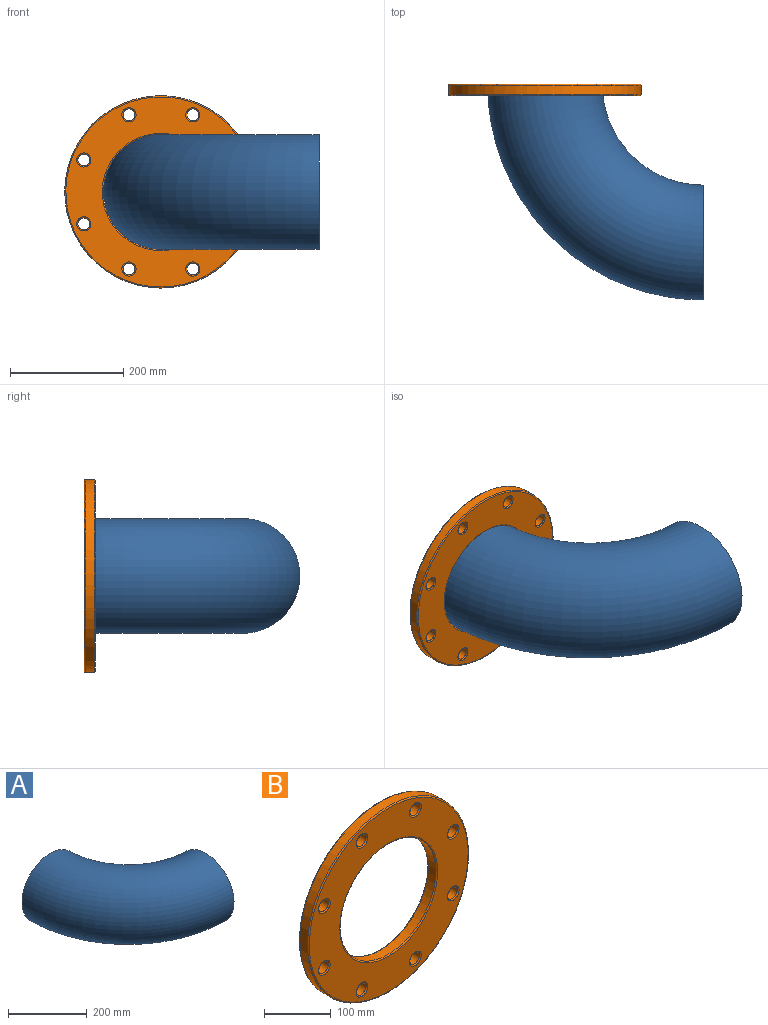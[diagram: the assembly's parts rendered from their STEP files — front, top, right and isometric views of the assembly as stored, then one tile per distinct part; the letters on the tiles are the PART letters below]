
ASSEMBLY  parts=2 mates=1
PART A: 4 faces, bbox 412.7x412.7x203 mm
  f0: torus R=279.76mm, axis (0,0,1), area 269205.5mm2, adj f1,f2
  f1: plane 203x203mm, normal (0,1,0), area 2500.7mm2, adj f0,f3
  f2: plane 203x203mm, normal (1,0,0), area 2500.7mm2, adj f0,f3
  f3: torus R=279.76mm, axis (0,0,1), area 280249.8mm2, adj f1,f2
PART B: 32 faces, bbox 368x20x368 mm
  f0: cylinder r=101.6mm len=203.2mm, axis (0,1,0), area 10213.9mm2, adj f20,f30
  f1: cylinder r=10.5mm len=21mm, axis (0,1,0), area 1055.6mm2, adj f19,f29
  f2: cylinder r=10.5mm len=21mm, axis (0,1,0), area 1055.6mm2, adj f18,f28
  f3: cylinder r=10.5mm len=21mm, axis (0,1,0), area 1055.6mm2, adj f17,f27
  f4: cylinder r=10.5mm len=21mm, axis (0,1,0), area 1055.6mm2, adj f16,f26
  f5: cylinder r=10.5mm len=21mm, axis (0,1,0), area 1055.6mm2, adj f15,f25
  f6: cylinder r=10.5mm len=21mm, axis (0,1,0), area 1055.6mm2, adj f14,f24
  f7: cylinder r=10.5mm len=21mm, axis (0,1,0), area 1055.6mm2, adj f13,f23
  f8: cylinder r=10.5mm len=21mm, axis (0,1,0), area 1055.6mm2, adj f12,f22
  f9: cylinder r=170mm len=340mm, axis (0,1,0), area 17090.3mm2, adj f21,f31
  f10: plane 336x336mm, normal (0,-1,0), area 51022.7mm2, adj f22,f23,f24,f25,f26,f27,f28,f29
  f11: plane 336x336mm, normal (0,1,0), area 51022.7mm2, adj f12,f13,f14,f15,f16,f17,f18,f19
  f12: torus R=12.5mm, axis (0,-1,0), area 221.6mm2, adj f8,f11
  f13: torus R=12.5mm, axis (0,-1,0), area 221.6mm2, adj f7,f11
  f14: torus R=12.5mm, axis (0,-1,0), area 221.6mm2, adj f6,f11
  f15: torus R=12.5mm, axis (0,-1,0), area 221.6mm2, adj f5,f11
  f16: torus R=12.5mm, axis (0,-1,0), area 221.6mm2, adj f4,f11
  f17: torus R=12.5mm, axis (0,-1,0), area 221.6mm2, adj f3,f11
  f18: torus R=12.5mm, axis (0,-1,0), area 221.6mm2, adj f2,f11
  f19: torus R=12.5mm, axis (0,-1,0), area 221.6mm2, adj f1,f11
  f20: torus R=103.6mm, axis (0,-1,0), area 2019.8mm2, adj f0,f11
  f21: torus R=168mm, axis (0,-1,0), area 3341.3mm2, adj f9,f11
  f22: torus R=12.5mm, axis (0,-1,0), area 221.6mm2, adj f8,f10
  f23: torus R=12.5mm, axis (0,-1,0), area 221.6mm2, adj f7,f10
  f24: torus R=12.5mm, axis (0,-1,0), area 221.6mm2, adj f6,f10
  f25: torus R=12.5mm, axis (0,-1,0), area 221.6mm2, adj f5,f10
  f26: torus R=12.5mm, axis (0,-1,0), area 221.6mm2, adj f4,f10
  f27: torus R=12.5mm, axis (0,-1,0), area 221.6mm2, adj f3,f10
  f28: torus R=12.5mm, axis (0,-1,0), area 221.6mm2, adj f2,f10
  f29: torus R=12.5mm, axis (0,-1,0), area 221.6mm2, adj f1,f10
  f30: torus R=103.6mm, axis (0,-1,0), area 2019.8mm2, adj f0,f10
  f31: torus R=168mm, axis (0,-1,0), area 3341.3mm2, adj f9,f10
PLACE A at identity
PLACE B at identity
MATE fastened B.f0 <-> A.f1  axis (0,1,0) through (0,0,0)mm
